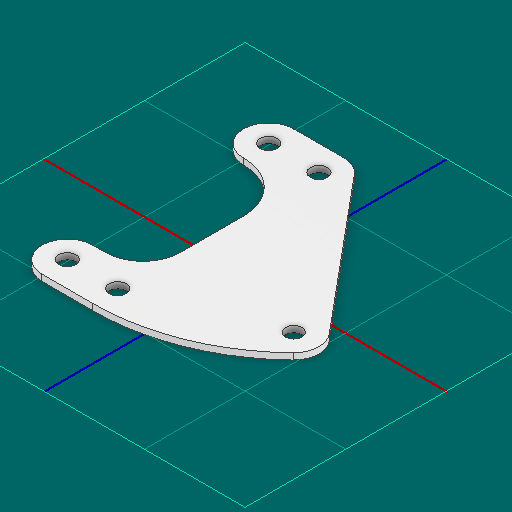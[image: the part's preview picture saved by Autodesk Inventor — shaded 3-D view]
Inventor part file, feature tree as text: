
AUTODESK INVENTOR PART (.ipt)
format: ipt  version: 2025 (Build 290162000, 162)  size: 140,288 bytes
history: native  units: in
note: dims shown in document units (in); Inventor stores cm internally (conversion verified against a paired STEP export)
features: other x5, sketch x1
ambient origin geometry x8: Origin, YZ Plane, XZ Plane, XY Plane, X Axis, Y Axis, Z Axis, Center Point
bodies: Solid1 (feature_tree)
feature tree (6):
  other  "gusset.ipt"
  other  "Blocks"
  other  "main"
  other  "Solid1::gusset.ipt"
  other  "TaggingFeature1"
  sketch  "Sketch1"  dims[d0=0.3937in d1=0.5in d2=0.375in]
